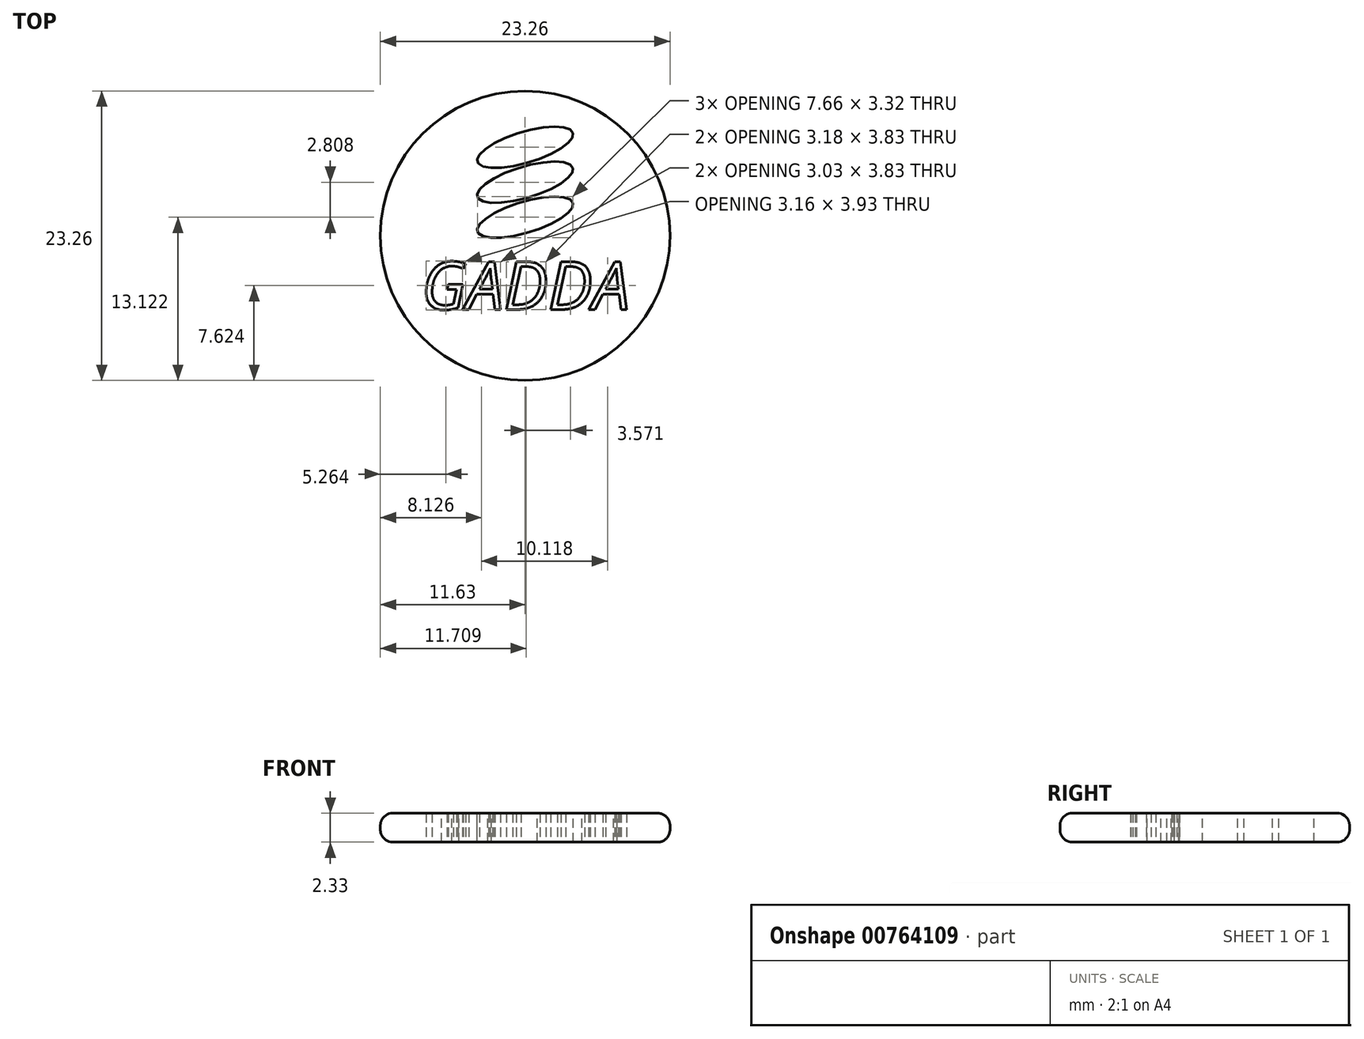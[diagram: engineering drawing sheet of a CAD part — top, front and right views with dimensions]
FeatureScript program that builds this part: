
annotation { "Feature Type Name" : "Feature", "Feature Type Description" : "" }
export const myFeature = defineFeature(function(context is Context, id is Id, definition is map)
    precondition{}
    {
        {
            assignVariable(context, id + "F0", {"name" : "SPES", "anyValue" : 2.33});
        }
        {
            var Q0;
            Q0=qCreatedBy(makeId("Top.planeOp"),FACE);
            var sketch = newSketch(context, id + "F1", { "sketchPlane" : qUnion([Q0])});
            skCircle(sketch, "E0", {"center": v(0, 0) * mm, "radius": 11.62 * mm});
            skSolve(sketch);
        }
        {
            var Q0;
            Q0=makeQuery(id+"F1.imprint","IMPRINT",FACE,{"disambiguationData":[TD([[makeQuery(id+"F1.imprint","IMPRINT",EDGE,{"derivedFrom":sQuery(id+"F1.wireOp",EDGE,"E0")}),1.0]])]});
            extrude(context, id + "F2", {"entities" : qUnion([Q0]), "depth" : 2.33 * mm, "offsetDistance" : 25 * mm});
        }
        {
            var Q0;
            Q0=makeQuery(id+"F2.opExtrude","CAP_EDGE",EDGE,{"disambiguationData":[OSD([sQuery(id+"F1.wireOp",EDGE,"E0")])],"isStart":true});
            var Q1;
            Q1=makeQuery(id+"F2.opExtrude","CAP_EDGE",EDGE,{"disambiguationData":[OSD([sQuery(id+"F1.wireOp",EDGE,"E0")])],"isStart":false});
            fillet(context, id + "F3", {"entities" : qUnion([Q0, Q1]), "radius" : 1 * mm, "tangentPropagation" : true, "allowEdgeOverflow" : false});
        }
        {
            var Q0;
            Q0=qCreatedBy(makeId("Top.planeOp"),FACE);
            var sketch = newSketch(context, id + "F4", { "sketchPlane" : qUnion([Q0])});
            skText(sketch, "E1", { "text": "GADDA", "fontName": "OpenSans-Italic.ttf"});
            const initialGuessF4  = {"E1": [-0.00834, -0.00592, 1, 0, 0.00386]};
            skSetInitialGuess(sketch, initialGuessF4);
            skSolve(sketch);
        }
        {
            var Q0;
            {var subQ0=sQuery(id+"F1.wireOp",EDGE,"E0");Q0=makeQuery(id+"FliUfrnVAcBvgtl_1.boolean.opBoolean","SPLIT",FACE,{"disambiguationData":[TD([makeQuery(id+"FliUfrnVAcBvgtl_1.opExtrude","SWEPT_FACE",FACE,{"disambiguationData":[OSD([sQuery(id+"FjR9lfXDtQEPAwO_1.wireOp",EDGE,"85ffe3c2-55fe-49f6-81ed-dfd63056ef19.sketch_text.stroke-0")])]})])],"derivedFrom":makeQuery(id+"F2.opExtrude","CAP_FACE",FACE,{"disambiguationData":[OSD([subQ0])],"isStart":false})});}
            var sketch = newSketch(context, id + "F5", { "sketchPlane" : qUnion([Q0])});
            skEllipse(sketch, "E2", {"center": v(0, 7.1) * mm, "majorRadius": 4 * mm, "minorRadius": 1.25 * mm, "majorAxis": v(0.96, 0.29)});
            skEllipse(sketch, "E3.1.0.0", {"center": v(0, 4.3) * mm, "majorRadius": 4 * mm, "minorRadius": 1.25 * mm, "majorAxis": v(0.96, 0.29)});
            skEllipse(sketch, "E3.2.0.0", {"center": v(0, 1.5) * mm, "majorRadius": 4 * mm, "minorRadius": 1.25 * mm, "majorAxis": v(0.96, 0.29)});
            skLineSegment(sketch, "E3.direction1", {"start": v(0, 7.1) * mm, "end": v(0, 4.3) * mm, "construction": true});
            skSolve(sketch);
        }
        {
            var Q0;
            Q0 = qSketchRegion(id + "F4", true);
            extrude(context, id + "F6", {"entities" : qUnion([Q0]), "operationType" : NewBodyOperationType.REMOVE, "endBound" : BoundingType.UP_TO_NEXT, "depth" : 25 * mm, "offsetDistance" : 25 * mm});
        }
        {
            var Q0;
            Q0=makeQuery(id+"F5.imprint","IMPRINT",FACE,{"disambiguationData":[TD([[makeQuery(id+"F5.imprint","IMPRINT",EDGE,{"derivedFrom":sQuery(id+"F5.wireOp",EDGE,"E2")}),1.0]])]});
            var Q1;
            Q1=makeQuery(id+"F5.imprint","IMPRINT",FACE,{"disambiguationData":[TD([[makeQuery(id+"F5.imprint","IMPRINT",EDGE,{"derivedFrom":sQuery(id+"F5.wireOp",EDGE,"E3.1.0.0")}),1.0]])]});
            var Q2;
            Q2=makeQuery(id+"F5.imprint","IMPRINT",FACE,{"disambiguationData":[TD([[makeQuery(id+"F5.imprint","IMPRINT",EDGE,{"derivedFrom":sQuery(id+"F5.wireOp",EDGE,"E3.2.0.0")}),1.0]])]});
            var Q3;
            Q3=sQuery(id+"F5.wireOp",EDGE,"E2");
            var Q4;
            Q4=sQuery(id+"F5.wireOp",EDGE,"E3.1.0.0");
            var Q5;
            Q5=sQuery(id+"F5.wireOp",EDGE,"E3.2.0.0");
            extrude(context, id + "F7", {"entities" : qUnion([Q0, Q1, Q2]), "operationType" : NewBodyOperationType.REMOVE, "surfaceEntities" : qUnion([Q3, Q4, Q5]), "endBound" : BoundingType.UP_TO_NEXT, "oppositeDirection" : true, "depth" : (getVariable(context, 'SPES')) * mm, "offsetDistance" : 25 * mm});
        }
    });
